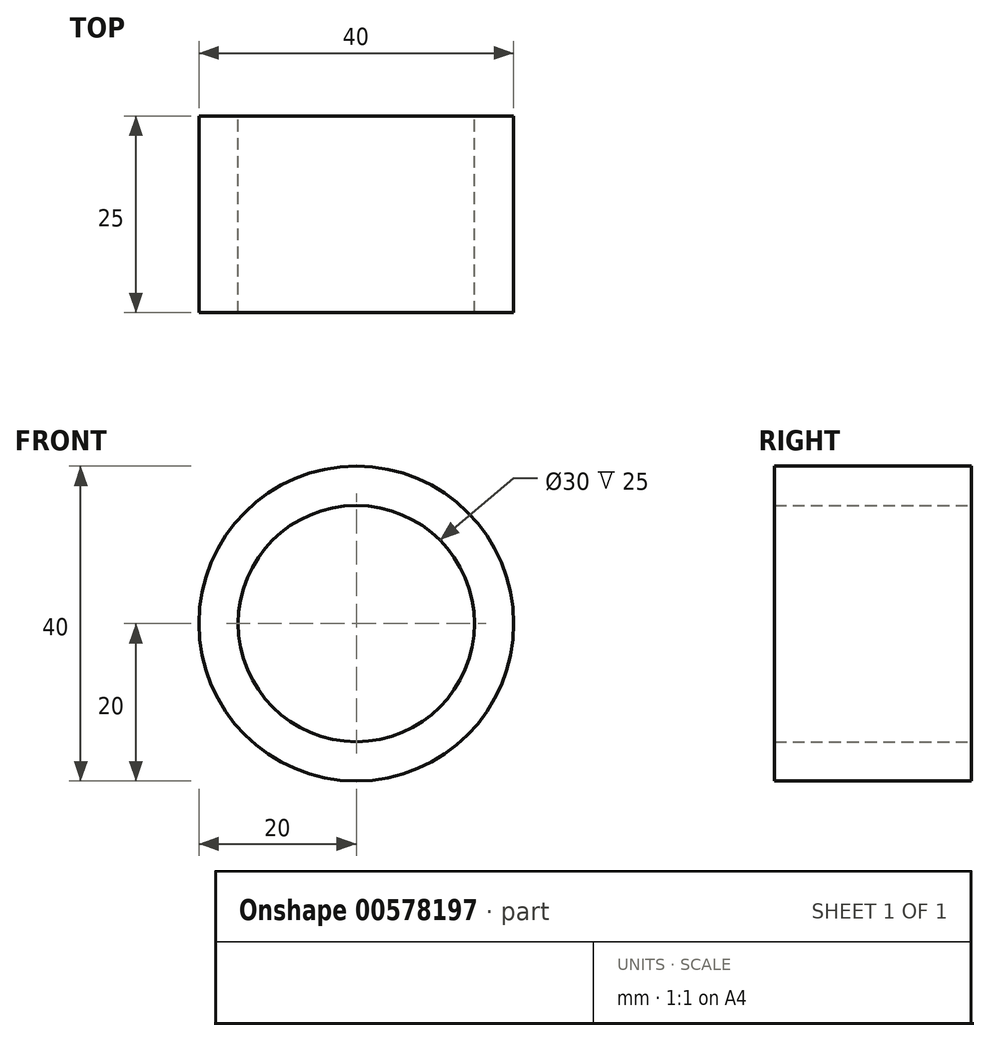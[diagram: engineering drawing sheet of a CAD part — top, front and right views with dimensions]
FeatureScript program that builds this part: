
annotation { "Feature Type Name" : "Feature", "Feature Type Description" : "" }
export const myFeature = defineFeature(function(context is Context, id is Id, definition is map)
    precondition{}
    {
        {
            var Q0;
            Q0=qCreatedBy(makeId("Front.planeOp"),FACE);
            var sketch = newSketch(context, id + "F0", { "sketchPlane" : qUnion([Q0])});
            skCircle(sketch, "E0", {"center": v(0, 0) * mm, "radius": 20 * mm});
            skCircle(sketch, "E1", {"center": v(0, 0) * mm, "radius": 15 * mm});
            skSolve(sketch);
        }
        {
            var Q0;
            Q0=makeQuery(id+"F0.imprint","IMPRINT",FACE,{"disambiguationData":[TD([[makeQuery(id+"F0.imprint","IMPRINT",EDGE,{"derivedFrom":sQuery(id+"F0.wireOp",EDGE,"E0")}),1.0]])]});
            extrude(context, id + "F1", {"entities" : qUnion([Q0]), "depth" : 25 * mm, "offsetDistance" : 25 * mm});
        }
    });
